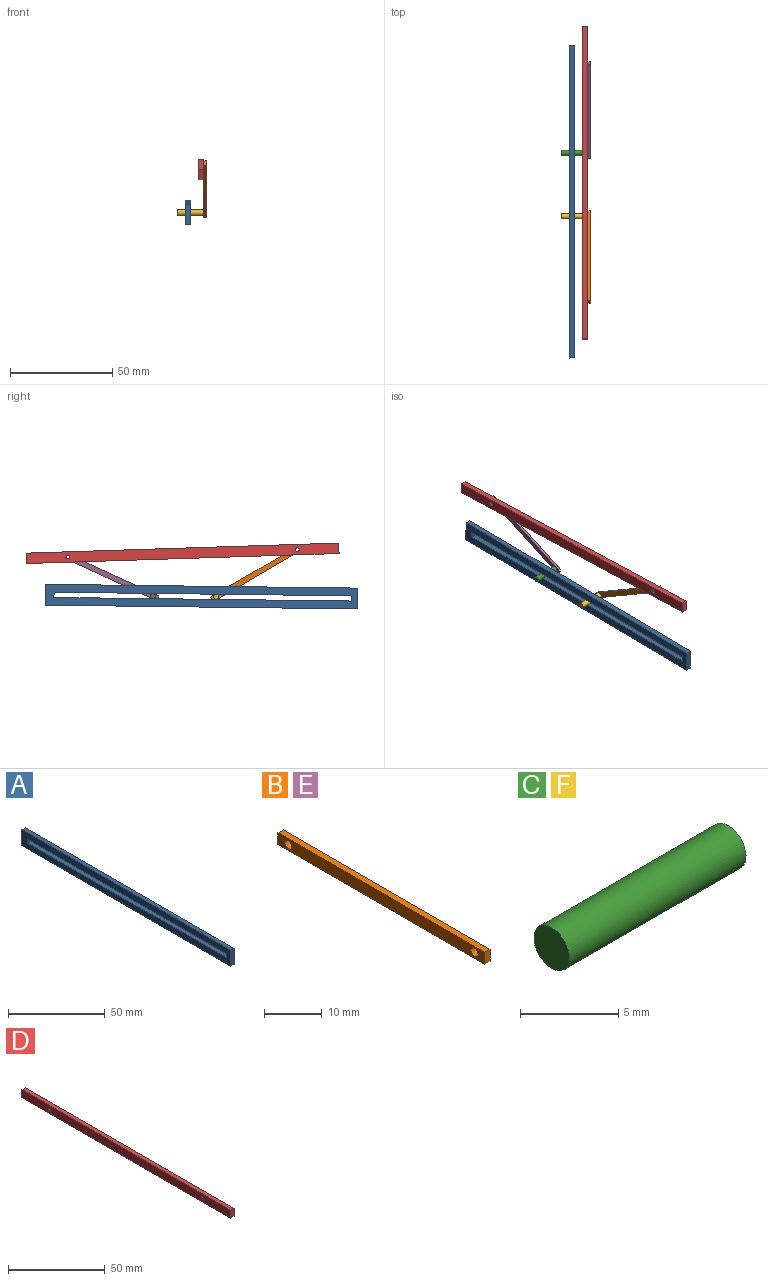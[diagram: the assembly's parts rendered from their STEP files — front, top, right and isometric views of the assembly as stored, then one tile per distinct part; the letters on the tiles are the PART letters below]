
ASSEMBLY  parts=6 mates=6
PART A: 10 faces, bbox 2.5x152.4x10.2 mm
  f0: plane 152.4x2.54mm, normal (0,0,1), area 387.1mm2, adj f1,f7,f8,f9
  f1: plane 10.16x2.54mm, normal (0,-1,0), area 25.8mm2, adj f0,f2,f8,f9
  f2: plane 152.4x2.54mm, normal (0,0,-1), area 387.1mm2, adj f1,f7,f8,f9
  f3: plane 2.54x2.54mm, normal (0,1,0), area 6.5mm2, adj f4,f6,f8,f9
  f4: plane 145.12x2.54mm, normal (0,0,-1), area 368.6mm2, adj f3,f5,f8,f9
  f5: plane 2.54x2.54mm, normal (0,-1,0), area 6.5mm2, adj f4,f6,f8,f9
  f6: plane 145.12x2.54mm, normal (0,0,1), area 368.6mm2, adj f3,f5,f8,f9
  f7: plane 10.16x2.54mm, normal (0,1,0), area 25.8mm2, adj f0,f2,f8,f9
  f8: plane 152.4x10.16mm, normal (1,0,0), area 1179.8mm2, adj f0,f1,f2,f3,f4,f5,f6,f7
  f9: plane 152.4x10.16mm, normal (-1,0,0), area 1179.8mm2, adj f0,f1,f2,f3,f4,f5,f6,f7
PART B: 8 faces, bbox 1.3x50.8x2.5 mm
  f0: plane 50.8x1.27mm, normal (0,0,1), area 64.5mm2, adj f1,f5,f6,f7
  f1: plane 2.54x1.27mm, normal (0,-1,0), area 3.2mm2, adj f0,f2,f6,f7
  f2: plane 50.8x1.27mm, normal (0,0,-1), area 64.5mm2, adj f1,f5,f6,f7
  f3: cylinder r=0.89mm len=1.78mm, axis (-1,0,0), area 7.1mm2, adj f6,f7
  f4: cylinder r=0.89mm len=1.78mm, axis (-1,0,0), area 7.1mm2, adj f6,f7
  f5: plane 2.54x1.27mm, normal (0,1,0), area 3.2mm2, adj f0,f2,f6,f7
  f6: plane 50.8x2.54mm, normal (1,0,0), area 124mm2, adj f0,f1,f2,f3,f4,f5
  f7: plane 50.8x2.54mm, normal (-1,0,0), area 124mm2, adj f0,f1,f2,f3,f4,f5
PART C: 3 faces, bbox 12.7x2.5x2.5 mm
  f0: cylinder r=1.27mm len=12.7mm, axis (-1,0,0), area 101.3mm2, adj f1,f2
  f1: plane 2.54x2.54mm, normal (1,0,0), area 5.1mm2, adj f0
  f2: plane 2.54x2.54mm, normal (-1,0,0), area 5.1mm2, adj f0
PART D: 8 faces, bbox 2.5x152.6x5.1 mm
  f0: plane 152.65x2.54mm, normal (0,0,1), area 387.7mm2, adj f1,f5,f6,f7
  f1: plane 5.08x2.54mm, normal (0,-1,0), area 12.9mm2, adj f0,f2,f6,f7
  f2: plane 152.65x2.54mm, normal (0,0,-1), area 387.7mm2, adj f1,f5,f6,f7
  f3: cylinder r=0.89mm len=2.54mm, axis (-1,0,0), area 14.2mm2, adj f6,f7
  f4: cylinder r=0.89mm len=2.54mm, axis (-1,0,0), area 14.2mm2, adj f6,f7
  f5: plane 5.08x2.54mm, normal (0,1,0), area 12.9mm2, adj f0,f2,f6,f7
  f6: plane 152.65x5.08mm, normal (1,0,0), area 770.5mm2, adj f0,f1,f2,f3,f4,f5
  f7: plane 152.65x5.08mm, normal (-1,0,0), area 770.5mm2, adj f0,f1,f2,f3,f4,f5
PART E: same geometry as B
PART F: same geometry as C
PLACE A rot(axis=(1,0,0),0.7deg) t=(5.21,-78.24,-33.09)mm fixed
PLACE B rot(axis=(1,0,0),149.8deg) t=(14.1,-112.72,33.04)mm
PLACE C rot(axis=(1,0,0),0.7deg) t=(1.4,9.44,-42.84)mm
PLACE D rot(axis=(-1,0,0),1.8deg) t=(11.56,-69.67,-46.1)mm
PLACE E rot(axis=(-1,0,0),155.4deg) t=(14.1,-82.74,1.88)mm
PLACE F rot(axis=(1,0,0),0.7deg) t=(1.4,-21.44,-43.21)mm
MATE revolute D.f3 <-> B.f4  axis (1,0,0) through (14.1,-124.71,-10.16)mm
MATE planar A.f8 <-> F.f0  axis (1,0,0) through (7.75,-77.93,-33.09)mm
MATE revolute D.f4 <-> E.f3  axis (1,0,0) through (14.1,-12.76,-13.76)mm
MATE revolute B.f3 <-> F.f0  axis (-1,0,0) through (14.1,-85.21,-33.17)mm
MATE planar A.f8 <-> C.f0  axis (1,0,0) through (7.75,-77.93,-33.09)mm
MATE revolute E.f4 <-> C.f0  axis (-1,0,0) through (14.1,-54.33,-32.8)mm
